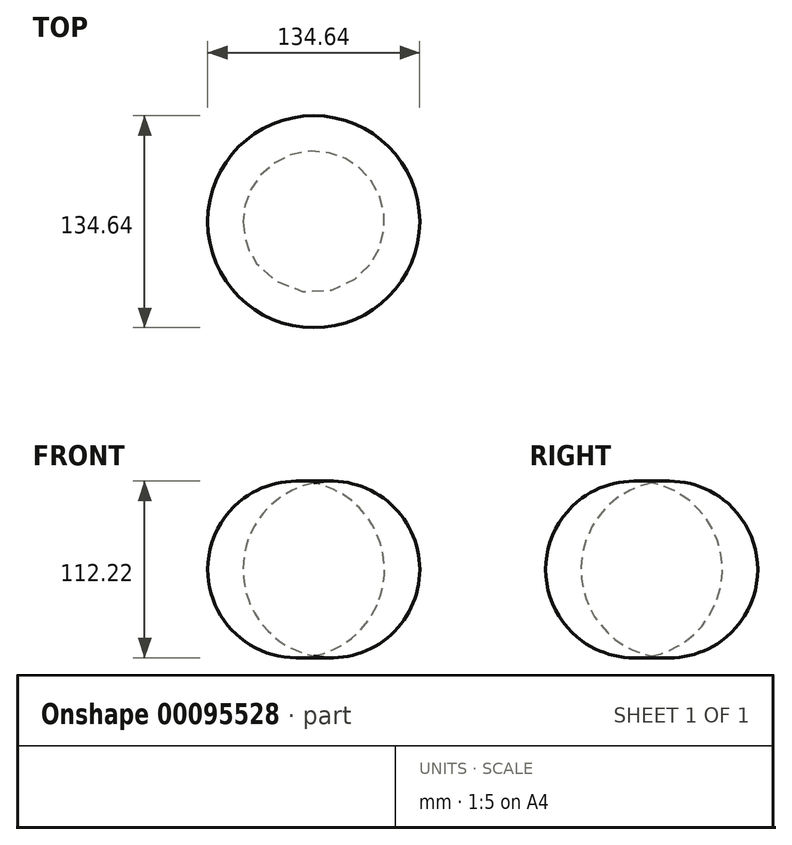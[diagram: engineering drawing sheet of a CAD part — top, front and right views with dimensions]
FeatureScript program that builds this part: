
annotation { "Feature Type Name" : "Feature", "Feature Type Description" : "" }
export const myFeature = defineFeature(function(context is Context, id is Id, definition is map)
    precondition{}
    {
        {
            var Q0;
            Q0=qCreatedBy(makeId("Front.planeOp"),FACE);
            var sketch = newSketch(context, id + "F0", { "sketchPlane" : qUnion([Q0])});
            skLineSegment(sketch, "E0", {"start": v(-45.9, 60.04) * mm, "end": v(-45.9, -49.91) * mm});
            skArc(sketch, "E1", {"start": v(-45.9, -49.91) * mm, "mid": v(-1, 5.07) * mm, "end": v(-45.9, 60.04) * mm});
            skSolve(sketch);
        }
        {
            var Q0;
            Q0=makeQuery(id+"F0.imprint","IMPRINT",FACE,{"disambiguationData":[TD([[makeQuery(id+"F0.imprint","IMPRINT",EDGE,{"derivedFrom":sQuery(id+"F0.wireOp",EDGE,"E0")}),1.0]])]});
            var Q1;
            Q1=sQuery(id+"F0.wireOp",EDGE,"E0");
            revolve(context, id + "F1", {"entities" : qUnion([Q0]), "axis" : qUnion([Q1]), "revolveType" : RevolveType.FULL});
        }
    });
